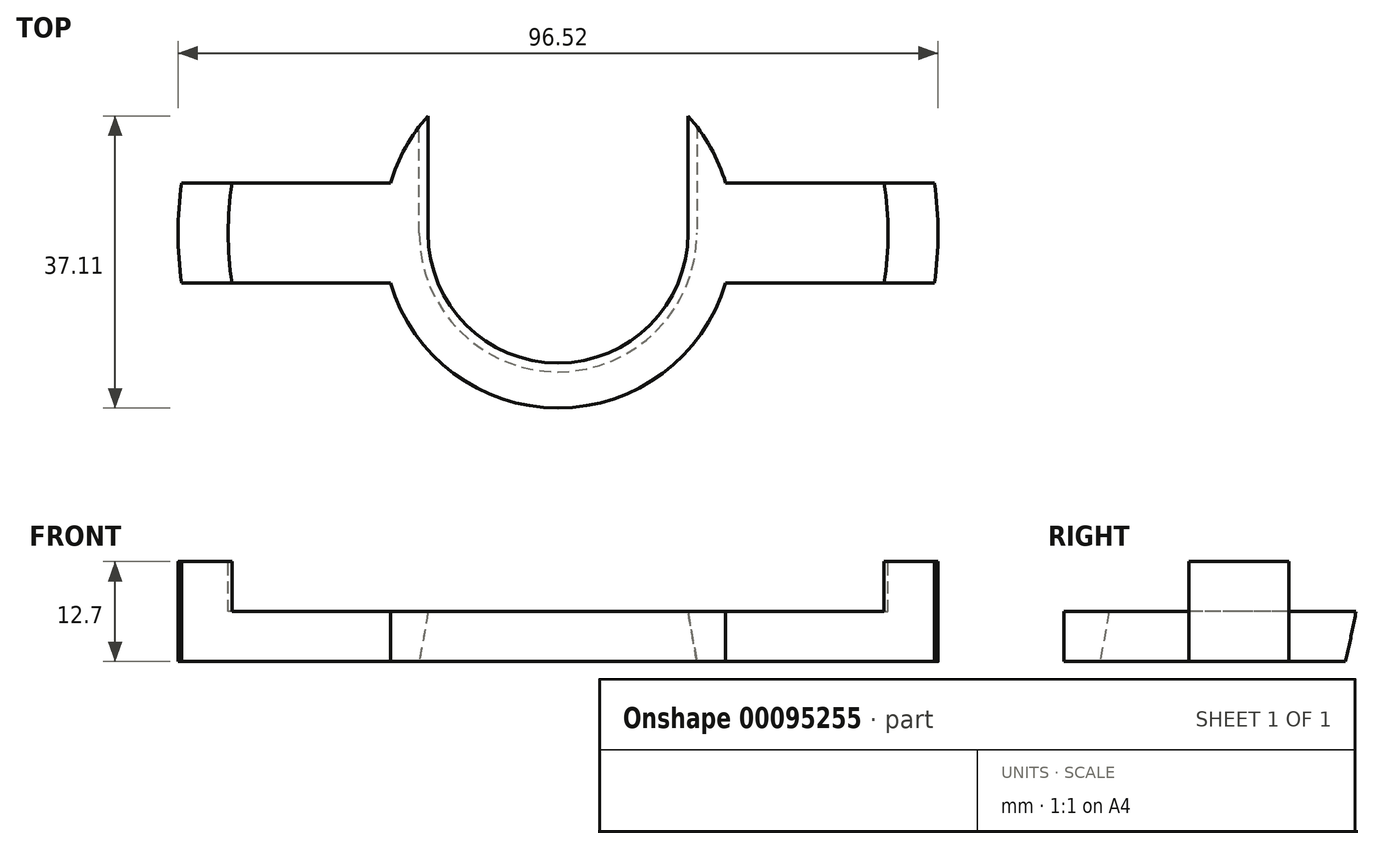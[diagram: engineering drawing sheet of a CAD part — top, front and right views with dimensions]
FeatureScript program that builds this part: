
annotation { "Feature Type Name" : "Feature", "Feature Type Description" : "" }
export const myFeature = defineFeature(function(context is Context, id is Id, definition is map)
    precondition{}
    {
        {
            var Q0;
            Q0=qCreatedBy(makeId("Top.planeOp"),FACE);
            var sketch = newSketch(context, id + "F0", { "sketchPlane" : qUnion([Q0])});
            skCircle(sketch, "E0", {"center": v(0, 0) * mm, "radius": 48.26 * mm});
            skLineSegment(sketch, "E1", {"start": v(-47.84, 6.35) * mm, "end": v(47.84, 6.35) * mm});
            skLineSegment(sketch, "E2", {"start": v(-47.84, -6.35) * mm, "end": v(47.84, -6.35) * mm});
            skCircle(sketch, "E3", {"center": v(0, 0) * mm, "radius": 22.23 * mm});
            skSolve(sketch);
        }
        {
            var Q0;
            {var subQ0=sQuery(id+"F0.wireOp",EDGE,"E1");Q0=makeQuery(id+"F0.imprint","IMPRINT",FACE,{"disambiguationData":[TD([[makeQuery(id+"F0.imprint","IMPRINT",EDGE,{"derivedFrom":subQ0}),-1.0]])]});}
            var Q1;
            {var subQ0=sQuery(id+"F0.wireOp",EDGE,"E3");var subQ1=sQuery(id+"F0.wireOp",EDGE,"E2");var subQ2=makeQuery(id+"F0.imprint","INTERSECT",VERTEX,{"disambiguationData":[OD(0.0)],"derivedFrom":[subQ1,subQ0]});Q1=makeQuery(id+"F0.imprint","IMPRINT",FACE,{"disambiguationData":[TD([[makeQuery(id+"F0.imprint","IMPRINT",EDGE,{"disambiguationData":[TD([[subQ2,-1.0]])],"derivedFrom":subQ1}),-1.0]])]});}
            var Q2;
            {var subQ0=sQuery(id+"F0.wireOp",EDGE,"E3");var subQ1=sQuery(id+"F0.wireOp",EDGE,"E1");var subQ2=makeQuery(id+"F0.imprint","INTERSECT",VERTEX,{"disambiguationData":[OD(0.0)],"derivedFrom":[subQ1,subQ0]});Q2=makeQuery(id+"F0.imprint","IMPRINT",FACE,{"disambiguationData":[TD([[makeQuery(id+"F0.imprint","IMPRINT",EDGE,{"disambiguationData":[TD([[subQ2,-1.0]])],"derivedFrom":subQ1}),1.0]])]});}
            extrude(context, id + "F1", {"entities" : qUnion([Q0, Q1, Q2]), "depth" : 12.7 * mm});
        }
        {
            var Q0;
            Q0=makeQuery(id+"F1.opExtrude","CAP_FACE",FACE,{"disambiguationData":[OSD([sQuery(id+"F0.wireOp",EDGE,"E0"),sQuery(id+"F0.wireOp",EDGE,"E1"),sQuery(id+"F0.wireOp",EDGE,"E2")])],"isStart":false});
            var sketch = newSketch(context, id + "F2", { "sketchPlane" : qUnion([Q0])});
            skCircle(sketch, "E4", {"center": v(0, 0) * mm, "radius": 41.9 * mm});
            skSolve(sketch);
        }
        {
            var Q0;
            Q0 = qSketchRegion(id + "F2", true);
            extrude(context, id + "F3", {"entities" : qUnion([Q0]), "operationType" : NewBodyOperationType.REMOVE, "oppositeDirection" : true, "depth" : 6.35 * mm});
        }
        {
            var Q0;
            Q0=makeQuery(id+"F3.boolean.opBoolean","COPY",FACE,{"derivedFrom":makeQuery(id+"F3.opExtrude","CAP_FACE",FACE,{"disambiguationData":[OSD([sQuery(id+"F2.wireOp",EDGE,"E4")])],"isStart":false})});
            var sketch = newSketch(context, id + "F4", { "sketchPlane" : qUnion([Q0])});
            skCircle(sketch, "E5", {"center": v(0, 0) * mm, "radius": 16.51 * mm});
            skLineSegment(sketch, "E6", {"start": v(-16.51, 0) * mm, "end": v(-16.51, 14.88) * mm});
            skLineSegment(sketch, "E7", {"start": v(16.51, 0) * mm, "end": v(16.51, 14.88) * mm});
            skSolve(sketch);
        }
        {
            var Q0;
            {var subQ0=sQuery(id+"F4.wireOp",EDGE,"E6");Q0=makeQuery(id+"F4.imprint","IMPRINT",FACE,{"disambiguationData":[TD([[makeQuery(id+"F4.imprint","IMPRINT",EDGE,{"derivedFrom":subQ0}),-1.0]])]});}
            var Q1;
            {var subQ0=sQuery(id+"F4.wireOp",EDGE,"E5");var subQ1=makeQuery(id+"F4.imprint","INTERSECT",VERTEX,{"derivedFrom":[subQ0,sQuery(id+"F4.wireOp",EDGE,"E6")]});Q1=makeQuery(id+"F4.imprint","IMPRINT",FACE,{"disambiguationData":[TD([[makeQuery(id+"F4.imprint","IMPRINT",EDGE,{"disambiguationData":[TD([[subQ1,1.0]])],"derivedFrom":subQ0}),1.0]])]});}
            extrude(context, id + "F5", {"entities" : qUnion([Q0, Q1]), "operationType" : NewBodyOperationType.REMOVE, "endBound" : BoundingType.UP_TO_NEXT, "oppositeDirection" : true, "depth" : 25 * mm, "hasDraft" : true, "draftAngle" : 10 * degree});
        }
    });
